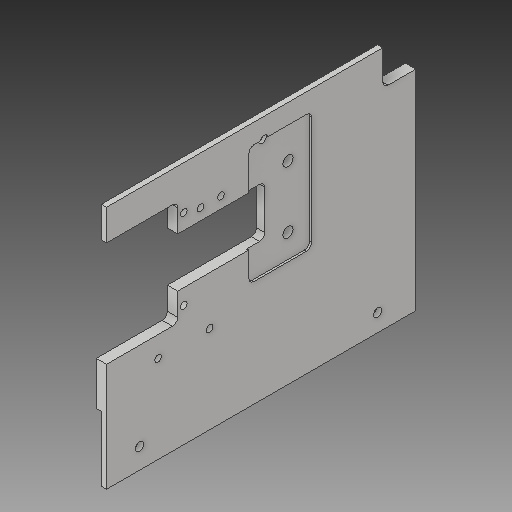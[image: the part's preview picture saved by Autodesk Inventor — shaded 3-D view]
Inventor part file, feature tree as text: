
AUTODESK INVENTOR PART (.ipt)
format: ipt  version: 2018 (Build 220112000, 112)  size: 227,840 bytes
history: native  units: mm
features: reference x9, extrude x8, sketch x8, other x7, fillet x2
ambient origin geometry x8: Origin, YZ Plane, XZ Plane, XY Plane, X Axis, Y Axis, Z Axis, Center Point
bodies: Solid1 (feature_tree)
feature tree (34):
  extrude  "Extrusion1"  Depth=237.0mm
  extrude  "Extrusion2"  Depth=32.0mm
  extrude  "Extrusion3"  Depth=5.0mm
  extrude  "Extrusion4"  Depth=138.0mm
  extrude  "Extrusion5"  Depth=61.0mm
  extrude  "Extrusion6"  Depth=5.0mm
  fillet  "Fillet1"  Radius=2.0mm
  extrude  "Extrusion7"  Depth=32.0mm
  fillet  "Fillet2"  Radius=20.0mm
  extrude  "Extrusion8"  Depth=10.0mm
  sketch  "Sketch1"  dims[d0=300.0mm d1=237.0mm]
  sketch  "Sketch2"  dims[d2=10.0mm d3=0.0mm d4=32.0mm]
  sketch  "Sketch3"  dims[d5=34.0mm d6=5.0mm]
  sketch  "Sketch4"  dims[d7=10.0mm d8=0.0mm d9=138.0mm]
  sketch  "Sketch5"  dims[d10=115.0mm d11=61.0mm]
  sketch  "Sketch6"  dims[d12=19.0mm d13=5.0mm d14=2.0mm d15=0.0mm]
  sketch  "Sketch7"  dims[d16=8.0mm d17=32.0mm d18=20.0mm]
  reference  "Reference1"
  reference  "Reference2"
  reference  "Reference3"
  sketch  "Sketch8"  dims[d19=17.0mm d20=37.0mm d21=153.0mm d22=20.0mm d23=2.0mm d24=0.0mm d25=70.0mm d26=63.0mm d27=63.0mm d28=67.0mm d29=5.0mm d30=0.0mm d31=122.0mm d32=10.0mm d34=60.0mm d35=51.0mm d36=5.0mm d37=0.0mm d38=5.0mm d39=30.0mm d40=102.0mm d41=57.0mm d42=10.0mm d43=48.0mm d44=10.0mm d45=0.0mm d46=5.0mm d47=10.0mm d48=0.0mm d49=0.25mm d50=0.25mm d51=0.25mm d52=0.25mm d53=0.25mm d54=0.25mm]
  reference  "Reference4"
  reference  "Reference5"
  reference  "Reference6"
  reference  "Reference7"
  reference  "Reference8"
  reference  "Reference9"
  parser-record x1  (decoder bookkeeping rows leaked as tree rows — omitted from the tree; the rows remain in map.json)
  other  "Lathe Model V3.iam"
  other  "MotorHolderLongAxis:1"
  other  "BNT 2010-2_6 +1166L C7T-J1K_10000KBK 15BF 15:1"
  other  "BK 15:1"
  other  "MotorHolderLongAxisBottom:1"
  other  "MotorHolderLongAxisTop:1"
note: 1 file-system path scrubbed to <path> (originals preserved in map.json)
